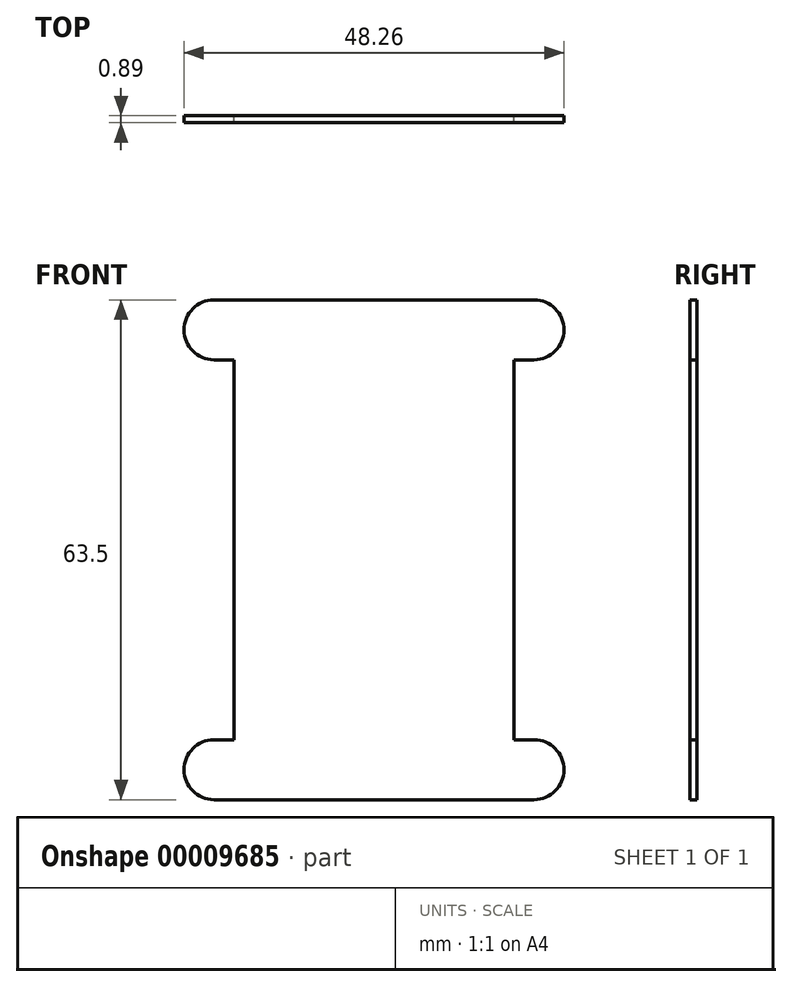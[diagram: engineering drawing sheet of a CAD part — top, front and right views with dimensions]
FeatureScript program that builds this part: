
annotation { "Feature Type Name" : "Feature", "Feature Type Description" : "" }
export const myFeature = defineFeature(function(context is Context, id is Id, definition is map)
    precondition{}
    {
        {
            var Q0;
            Q0=qCreatedBy(makeId("Front.planeOp"),FACE);
            var sketch = newSketch(context, id + "F0", { "sketchPlane" : qUnion([Q0])});
            skLineSegment(sketch, "E0", {"start": v(-17.78, 0) * mm, "end": v(-17.78, 24.13) * mm});
            skLineSegment(sketch, "E1.18.MirrorCS", {"start": v(-17.78, 0) * mm, "end": v(-17.78, 19.05) * mm});
            skLineSegment(sketch, "E2", {"start": v(-17.78, 24.13) * mm, "end": v(-20.32, 24.13) * mm});
            skLineSegment(sketch, "E3", {"start": v(-20.32, 24.13) * mm, "end": v(-20.32, 31.75) * mm, "construction": true});
            skLineSegment(sketch, "E4", {"start": v(-20.32, 31.75) * mm, "end": v(0, 31.75) * mm});
            skArc(sketch, "E5", {"start": v(-20.32, 31.75) * mm, "mid": v(-24.13, 27.94) * mm, "end": v(-20.32, 24.13) * mm});
            skLineSegment(sketch, "E6.0.MirrorCS", {"start": v(-17.78, 0) * mm, "end": v(-17.78, -24.13) * mm});
            skLineSegment(sketch, "E6.1.MirrorCS", {"start": v(-17.78, 0) * mm, "end": v(-17.78, -24.13) * mm});
            skLineSegment(sketch, "E6.2.MirrorCS", {"start": v(-17.78, 0) * mm, "end": v(-17.78, -24.13) * mm});
            skLineSegment(sketch, "E6.3.MirrorCS", {"start": v(-17.78, 0) * mm, "end": v(-17.78, -24.13) * mm});
            skLineSegment(sketch, "E6.4.MirrorCS", {"start": v(-17.78, 0) * mm, "end": v(-17.78, -24.13) * mm});
            skLineSegment(sketch, "E6.5.MirrorCS", {"start": v(-17.78, 0) * mm, "end": v(-17.78, -24.13) * mm});
            skLineSegment(sketch, "E6.6.MirrorCS", {"start": v(-17.78, -24.13) * mm, "end": v(-20.32, -24.13) * mm});
            skLineSegment(sketch, "E6.7.MirrorCS", {"start": v(-17.78, 0) * mm, "end": v(-17.78, -24.13) * mm});
            skLineSegment(sketch, "E6.8.MirrorCS", {"start": v(-17.78, 0) * mm, "end": v(-17.78, -19.05) * mm});
            skLineSegment(sketch, "E6.9.MirrorCS", {"start": v(-20.32, -24.13) * mm, "end": v(-20.32, -31.75) * mm, "construction": true});
            skArc(sketch, "E6.10.MirrorCS", {"start": v(-20.32, -31.75) * mm, "mid": v(-24.13, -27.94) * mm, "end": v(-20.32, -24.13) * mm});
            skLineSegment(sketch, "E6.11.MirrorCS", {"start": v(-20.32, -31.75) * mm, "end": v(0, -31.75) * mm});
            skLineSegment(sketch, "E7.0.MirrorCS", {"start": v(17.78, 0) * mm, "end": v(17.78, 24.13) * mm});
            skLineSegment(sketch, "E7.1.MirrorCS", {"start": v(17.78, 0) * mm, "end": v(17.78, -24.13) * mm});
            skLineSegment(sketch, "E7.2.MirrorCS", {"start": v(17.78, 0) * mm, "end": v(17.78, -24.13) * mm});
            skLineSegment(sketch, "E7.3.MirrorCS", {"start": v(17.78, 0) * mm, "end": v(17.78, 24.13) * mm});
            skLineSegment(sketch, "E7.4.MirrorCS", {"start": v(17.78, 0) * mm, "end": v(17.78, -24.13) * mm});
            skLineSegment(sketch, "E7.5.MirrorCS", {"start": v(17.78, 0) * mm, "end": v(17.78, 24.13) * mm});
            skLineSegment(sketch, "E7.6.MirrorCS", {"start": v(17.78, 0) * mm, "end": v(17.78, -24.13) * mm});
            skLineSegment(sketch, "E7.7.MirrorCS", {"start": v(17.78, 0) * mm, "end": v(17.78, 24.13) * mm});
            skLineSegment(sketch, "E7.8.MirrorCS", {"start": v(17.78, 0) * mm, "end": v(17.78, 24.13) * mm});
            skLineSegment(sketch, "E7.9.MirrorCS", {"start": v(17.78, 0) * mm, "end": v(17.78, -24.13) * mm});
            skLineSegment(sketch, "E7.10.MirrorCS", {"start": v(17.78, 0) * mm, "end": v(17.78, -24.13) * mm});
            skLineSegment(sketch, "E7.11.MirrorCS", {"start": v(17.78, 0) * mm, "end": v(17.78, 24.13) * mm});
            skLineSegment(sketch, "E7.12.MirrorCS", {"start": v(20.32, -24.13) * mm, "end": v(20.32, -31.75) * mm, "construction": true});
            skLineSegment(sketch, "E7.13.MirrorCS", {"start": v(17.78, 0) * mm, "end": v(17.78, 19.05) * mm});
            skArc(sketch, "E7.14.MirrorCS", {"start": v(20.32, -31.75) * mm, "mid": v(24.13, -27.94) * mm, "end": v(20.32, -24.13) * mm});
            skLineSegment(sketch, "E7.15.MirrorCS", {"start": v(20.32, -31.75) * mm, "end": v(0, -31.75) * mm});
            skLineSegment(sketch, "E7.16.MirrorCS", {"start": v(17.78, 0) * mm, "end": v(17.78, 24.13) * mm});
            skLineSegment(sketch, "E7.17.MirrorCS", {"start": v(17.78, 0) * mm, "end": v(17.78, -24.13) * mm});
            skLineSegment(sketch, "E7.18.MirrorCS", {"start": v(17.78, -24.13) * mm, "end": v(20.32, -24.13) * mm});
            skLineSegment(sketch, "E7.19.MirrorCS", {"start": v(17.78, 0) * mm, "end": v(17.78, -19.05) * mm});
            skLineSegment(sketch, "E7.20.MirrorCS", {"start": v(20.32, 24.13) * mm, "end": v(20.32, 31.75) * mm, "construction": true});
            skLineSegment(sketch, "E7.21.MirrorCS", {"start": v(17.78, 24.13) * mm, "end": v(20.32, 24.13) * mm});
            skLineSegment(sketch, "E7.22.MirrorCS", {"start": v(20.32, 31.75) * mm, "end": v(0, 31.75) * mm});
            skArc(sketch, "E7.23.MirrorCS", {"start": v(20.32, 31.75) * mm, "mid": v(24.13, 27.94) * mm, "end": v(20.32, 24.13) * mm});
            skSolve(sketch);
        }
        {
            var Q0;
            Q0 = qSketchRegion(id + "F0", true);
            extrude(context, id + "F1", {"entities" : qUnion([Q0]), "depth" : 0.89 * mm});
        }
    });
